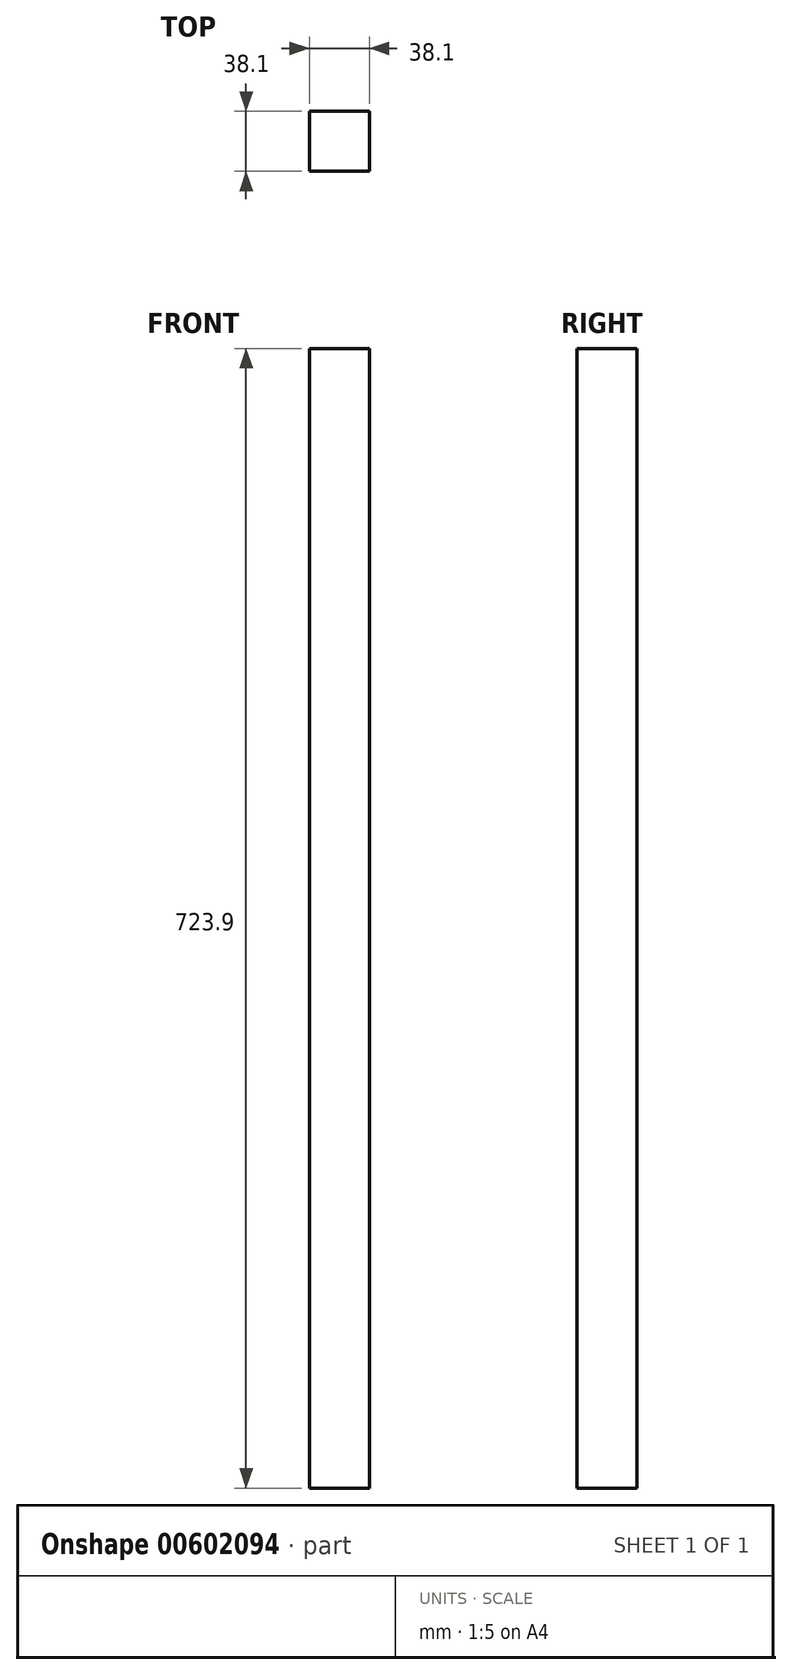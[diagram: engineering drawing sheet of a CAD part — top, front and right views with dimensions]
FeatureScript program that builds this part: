
annotation { "Feature Type Name" : "Feature", "Feature Type Description" : "" }
export const myFeature = defineFeature(function(context is Context, id is Id, definition is map)
    precondition{}
    {
        {
            var Q0;
            Q0=qCreatedBy(makeId("Top.planeOp"),FACE);
            var sketch = newSketch(context, id + "F0", { "sketchPlane" : qUnion([Q0])});
            skLineSegment(sketch, "E0.bottom", {"start": v(19.05, 19.05) * mm, "end": v(-19.05, 19.05) * mm});
            skLineSegment(sketch, "E0.top", {"start": v(19.05, -19.05) * mm, "end": v(-19.05, -19.05) * mm});
            skLineSegment(sketch, "E0.left", {"start": v(19.05, 19.05) * mm, "end": v(19.05, -19.05) * mm});
            skLineSegment(sketch, "E0.right", {"start": v(-19.05, 19.05) * mm, "end": v(-19.05, -19.05) * mm});
            skPoint(sketch, "E0.middle", {"position": v(0, 0) * mm});
            skSolve(sketch);
        }
        {
            var Q0;
            Q0=makeQuery(id+"F0.imprint","IMPRINT",FACE,{"disambiguationData":[TD([[makeQuery(id+"F0.imprint","IMPRINT",EDGE,{"derivedFrom":sQuery(id+"F0.wireOp",EDGE,"E0.bottom")}),1.0]])]});
            extrude(context, id + "F1", {"entities" : qUnion([Q0]), "depth" : 723.9 * mm, "offsetDistance" : 25.4 * mm});
        }
    });
